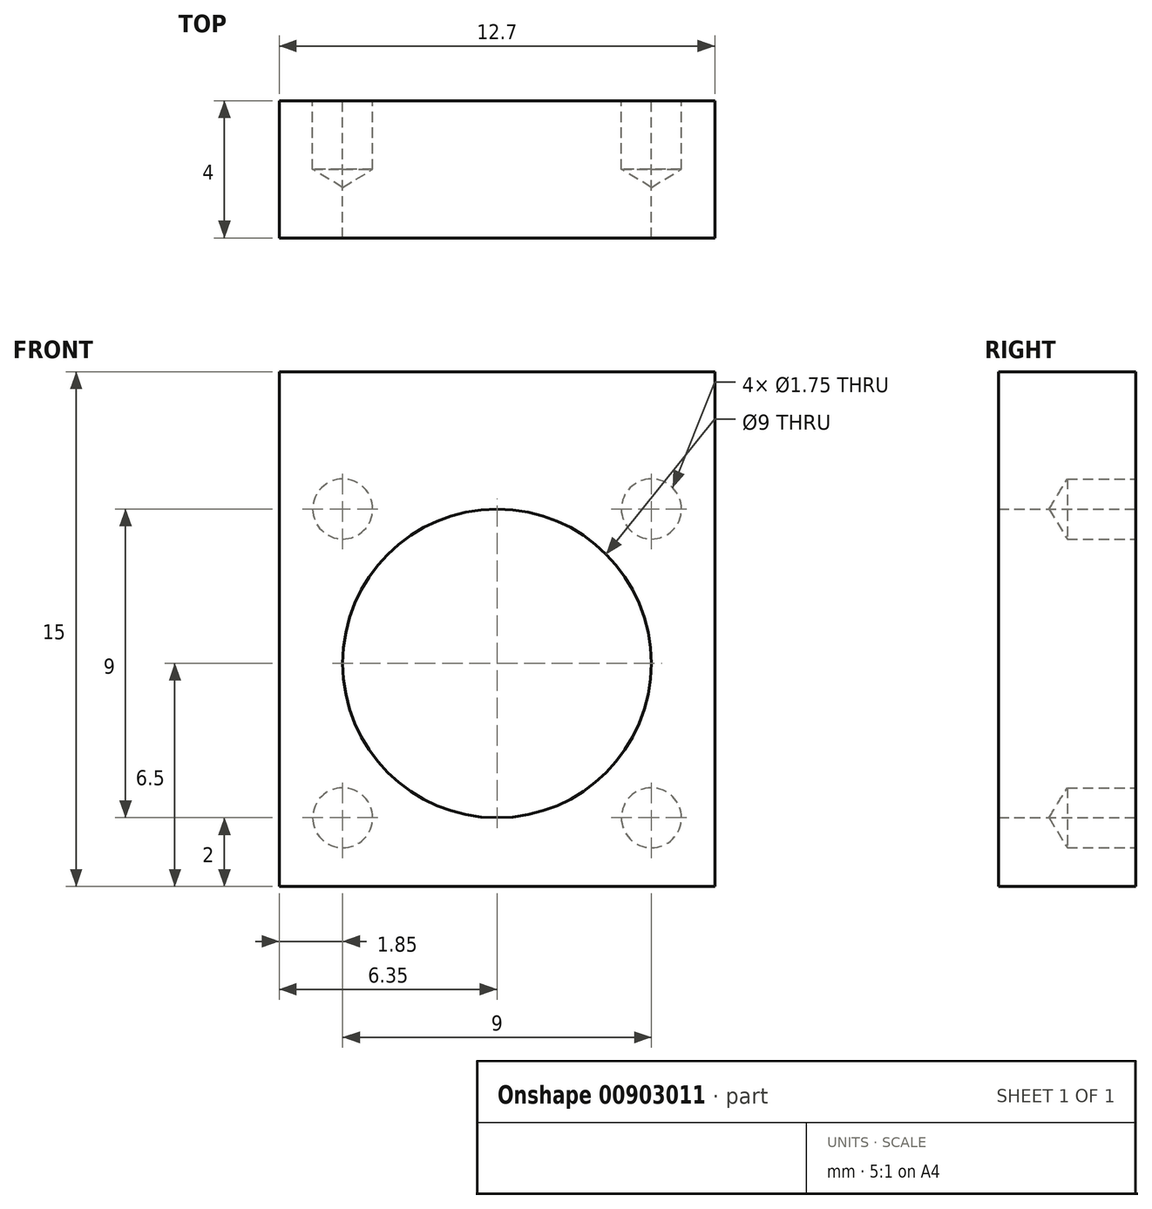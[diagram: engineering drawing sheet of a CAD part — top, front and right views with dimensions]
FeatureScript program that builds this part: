
annotation { "Feature Type Name" : "Feature", "Feature Type Description" : "" }
export const myFeature = defineFeature(function(context is Context, id is Id, definition is map)
    precondition{}
    {
        {
            var Q0;
            Q0=qCreatedBy(makeId("Front.planeOp"),FACE);
            var sketch = newSketch(context, id + "F0", { "sketchPlane" : qUnion([Q0])});
            skLineSegment(sketch, "E0.bottom", {"start": v(6.35, -6.5) * mm, "end": v(-6.35, -6.5) * mm});
            skLineSegment(sketch, "E0.top", {"start": v(6.35, 8.5) * mm, "end": v(-6.35, 8.5) * mm});
            skLineSegment(sketch, "E0.left", {"start": v(6.35, -6.5) * mm, "end": v(6.35, 8.5) * mm});
            skLineSegment(sketch, "E0.right", {"start": v(-6.35, -6.5) * mm, "end": v(-6.35, 8.5) * mm});
            skPoint(sketch, "E0.middle", {"position": v(0, 0) * mm});
            skCircle(sketch, "E1", {"center": v(0, 0) * mm, "radius": 4.5 * mm});
            skLineSegment(sketch, "E2.bottom", {"start": v(4.5, -4.5) * mm, "end": v(-4.5, -4.5) * mm, "construction": true});
            skLineSegment(sketch, "E2.top", {"start": v(4.5, 4.5) * mm, "end": v(-4.5, 4.5) * mm, "construction": true});
            skLineSegment(sketch, "E2.left", {"start": v(4.5, -4.5) * mm, "end": v(4.5, 4.5) * mm, "construction": true});
            skLineSegment(sketch, "E2.right", {"start": v(-4.5, -4.5) * mm, "end": v(-4.5, 4.5) * mm, "construction": true});
            skPoint(sketch, "E3", {"position": v(-4.5, 4.5) * mm});
            skPoint(sketch, "E4", {"position": v(4.5, 4.5) * mm});
            skPoint(sketch, "E5", {"position": v(4.5, -4.5) * mm});
            skPoint(sketch, "E6", {"position": v(-4.5, -4.5) * mm});
            skPoint(sketch, "E7", {"position": v(37.08, -8.95) * mm});
            skSolve(sketch);
        }
        {
            var Q0;
            Q0=makeQuery(id+"F0.imprint","IMPRINT",FACE,{"disambiguationData":[TD([[makeQuery(id+"F0.imprint","IMPRINT",EDGE,{"derivedFrom":sQuery(id+"F0.wireOp",EDGE,"E0.bottom")}),-1.0]])]});
            extrude(context, id + "F1", {"entities" : qUnion([Q0]), "depth" : 4 * mm, "offsetDistance" : 25 * mm});
        }
        {
            var Q0;
            Q0=sQuery(id+"F0.wireOp",VERTEX,"E3");
            var Q1;
            Q1=makeQuery(id+"F1.opExtrude","SWEPT_BODY",BODY,{"disambiguationData":[OSD([sQuery(id+"F0.wireOp",EDGE,"E0.bottom"),sQuery(id+"F0.wireOp",EDGE,"E0.top"),sQuery(id+"F0.wireOp",EDGE,"E0.left"),sQuery(id+"F0.wireOp",EDGE,"E0.right"),sQuery(id+"F0.wireOp",EDGE,"E1")])]});
            hole(context, id + "F2", {"style" : HoleStyle.SIMPLE, "endStyle" : HoleEndStyle.BLIND, "oppositeDirection" : true, "holeDiameter" : 1.75 * mm, "majorDiameter" : 5 * mm, "holeDepth" : 2 * mm, "isTappedThrough" : true, "tappedDepth" : 12 * mm, "tapClearance" : 3, "locations" : qUnion([Q0]), "scope" : qUnion([Q1])});
        }
        {
            var Q0;
            Q0=sQuery(id+"F0.wireOp",VERTEX,"E4");
            var Q1;
            Q1=sQuery(id+"F0.wireOp",VERTEX,"E5");
            var Q2;
            Q2=sQuery(id+"F0.wireOp",VERTEX,"E6");
            var Q3;
            Q3=makeQuery(id+"F1.opExtrude","SWEPT_BODY",BODY,{"disambiguationData":[OSD([sQuery(id+"F0.wireOp",EDGE,"E0.bottom"),sQuery(id+"F0.wireOp",EDGE,"E0.top"),sQuery(id+"F0.wireOp",EDGE,"E0.left"),sQuery(id+"F0.wireOp",EDGE,"E0.right"),sQuery(id+"F0.wireOp",EDGE,"E1")])]});
            hole(context, id + "F3", {"style" : HoleStyle.SIMPLE, "endStyle" : HoleEndStyle.BLIND, "oppositeDirection" : true, "holeDiameter" : 1.75 * mm, "majorDiameter" : 5 * mm, "holeDepth" : 2 * mm, "isTappedThrough" : true, "tappedDepth" : 12 * mm, "tapClearance" : 3, "locations" : qUnion([Q0, Q1, Q2]), "scope" : qUnion([Q3])});
        }
    });
